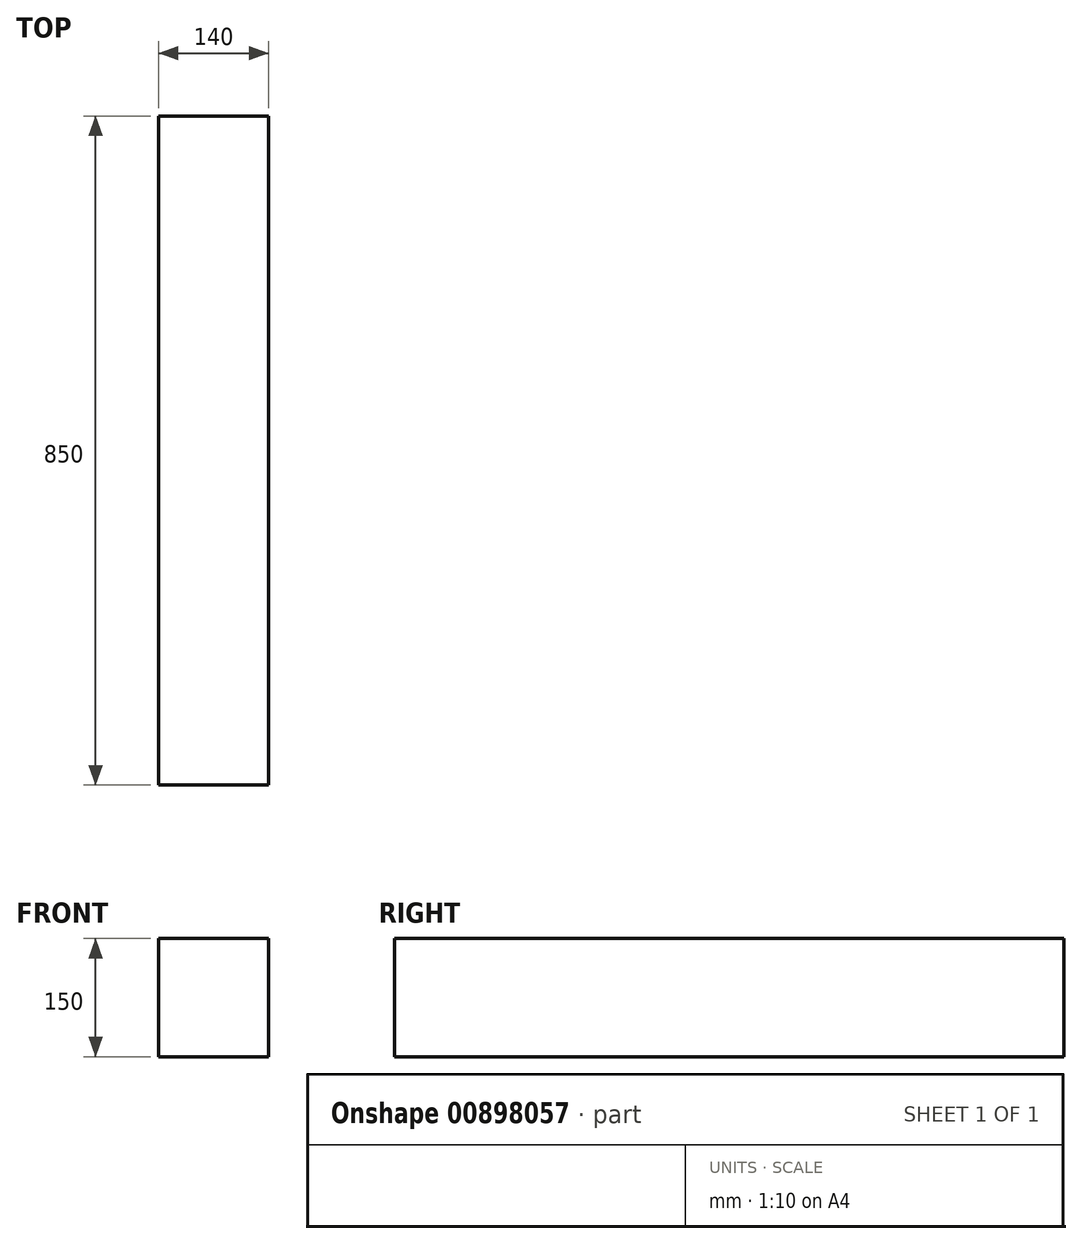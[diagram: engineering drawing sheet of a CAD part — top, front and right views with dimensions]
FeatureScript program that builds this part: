
annotation { "Feature Type Name" : "Feature", "Feature Type Description" : "" }
export const myFeature = defineFeature(function(context is Context, id is Id, definition is map)
    precondition{}
    {
        {
            var Q0;
            Q0=qCreatedBy(makeId("Front.planeOp"),FACE);
            var sketch = newSketch(context, id + "F0", { "sketchPlane" : qUnion([Q0])});
            skLineSegment(sketch, "E0", {"start": v(-74.74, -74.55) * mm, "end": v(65.4, -74.55) * mm});
            skLineSegment(sketch, "E1.bottom", {"start": v(-37.42, 108.67) * mm, "end": v(102.58, 108.67) * mm});
            skLineSegment(sketch, "E1.top", {"start": v(-37.42, -41.33) * mm, "end": v(102.58, -41.33) * mm});
            skLineSegment(sketch, "E1.left", {"start": v(-37.42, 108.67) * mm, "end": v(-37.42, -41.33) * mm});
            skLineSegment(sketch, "E1.right", {"start": v(102.58, 108.67) * mm, "end": v(102.58, -41.33) * mm});
            skSolve(sketch);
        }
        {
            var Q0;
            Q0=makeQuery(id+"F0.imprint","IMPRINT",FACE,{"disambiguationData":[TD([[makeQuery(id+"F0.imprint","IMPRINT",EDGE,{"derivedFrom":sQuery(id+"F0.wireOp",EDGE,"E1.bottom")}),-1.0]])]});
            extrude(context, id + "F1", {"entities" : qUnion([Q0]), "depth" : 850 * mm, "offsetDistance" : 25 * mm});
        }
    });
